AUTODESK INVENTOR PART (.ipt)
format: ipt  version: 2025.2 (Build 292293000, 293)  size: 278,528 bytes
history: native  units: mm
features: sketch x6
ambient origin geometry x8: Origin, YZ Plane, XZ Plane, XY Plane, X Axis, Y Axis, Z Axis, Center Point
feature tree (6):
  sketch  "Esboço Coincidente"
  sketch  "Esboço Colinear"
  sketch  "Esboço Paralelo"
  sketch  "Esboço Perpendicular"
  sketch  "Esboço HorVert"
  sketch  "Esboço Tangente"
